# Revit family: Loudspeaker_Bose_ArenaMatch-AMU105_with-U-Bracket_1
name_source: partatom
category: Communication Devices
revit_build: Autodesk Revit 2015 (Build: 20160512_0715(x64)
units: mm (PartAtom-declared; Revit-internal decimal feet)

## types (2) — shared parameters
Crossover = Passive (2.0 kHz crossover frequeuncy)
Default Elevation = 1219 mm
Depth = 229 mm
Description = Bose Professional ArenaMatch loudspeakers bring proven DeltaQ sound quality and flexibility to outdoor installations — sports stadiums, arenas, outdoor entertainment centers, and more.
Edition number = 1
Enviromental = IEC 60529 IP55 for outdoor, direct-exposure installations
Frequency Range = 90 Hz to 18 kHz
Frequency Response = 100 Hz to 16 kHz
HF Driver = 1 × Bose EMB2S extended high-frequency compression driver (2-inch voice coil)
Height = 152 mm
LF Driver = 1 × Bose LF5 high-excursion 5-inch woofer (2-inch voice coil)
Manufacturer = Bose Professional
Mounting/Suspension = 2x M8 threaded inserts for U-bracket; 2x M8 threaded inserts on rear (75 mm, 2-bolt pattern)
Nominal Coverage Pattern = 100° × 100°
Nominal Impedance = 8 Ω
Nominal Sensitivity = Bose Extended Lifecycle Test: Free field - 90 dB, Wall/Ceilling - 92 dB; AES Transducer Test: Free field - 90 dB, Wall/Ceilling - 92 dB;
Power Connector = 1x barrier strip, (accepts 10 to 18 wire gauge)
Power Handling(Long-term continuous) = Bose Extended Lifecycle Test: 100W; AES Transducer Test: 150W
Power Handling(peak) = Bose Extended Lifecycle Test: 400W; AES Transducer Test: 600W
Product Guid = fb344267-3e82-4ce6-a011-d9bf20c6c40a
Product data url = https://bimobject.com
Rated Maximum SPL = Calculated max. SPL @ 1 m (Bose power test) -  Free field: 110 dB, Wall/Ceilling: 112 dB ; Calculated max. SPL @ 1 m (2-hour power test) - Free field: 111 dB, Wall/Ceilling: 113 dB; Calculated max. SPL @ 1 m (Bose power test), peak - Free field: 116 dB, Wall/Ceilling: 118 dB; Calculated max. SPL @ 1 m (2-hour power test),
peak -Free field: 117 dB, Wall/Ceilling: 119 dB;
Recommended High-pass Filter = 90 Hz with minimum 12-dB / octave filter
Transformer Taps Information = 70V: 5, 10, 20, 40, 80 W; 100V: 10, 20, 40, 80 W
URL = https://pro.bose.com
Weight = 6.53 kg
Width = 305 mm

## per-type parameters (varying)
| type | Bracket Material | Grill Material | Product code | Speaker Material |
| 811433-0110 Black | Metal-Bose-Black | Grill-Bose-Black | 811433-0110 | Matt-Bose-Black |
| 811433-0210 White | Metal-Bose-White | Grill-Bose-White | 811433-0210 | Matt-Bose-White |

note: column(s) folded — value = type name in every type: Model

## geometry (parser evidence)
native form markers: Blend x4, Sweep x9
no freeform markers — native parametric forms only
